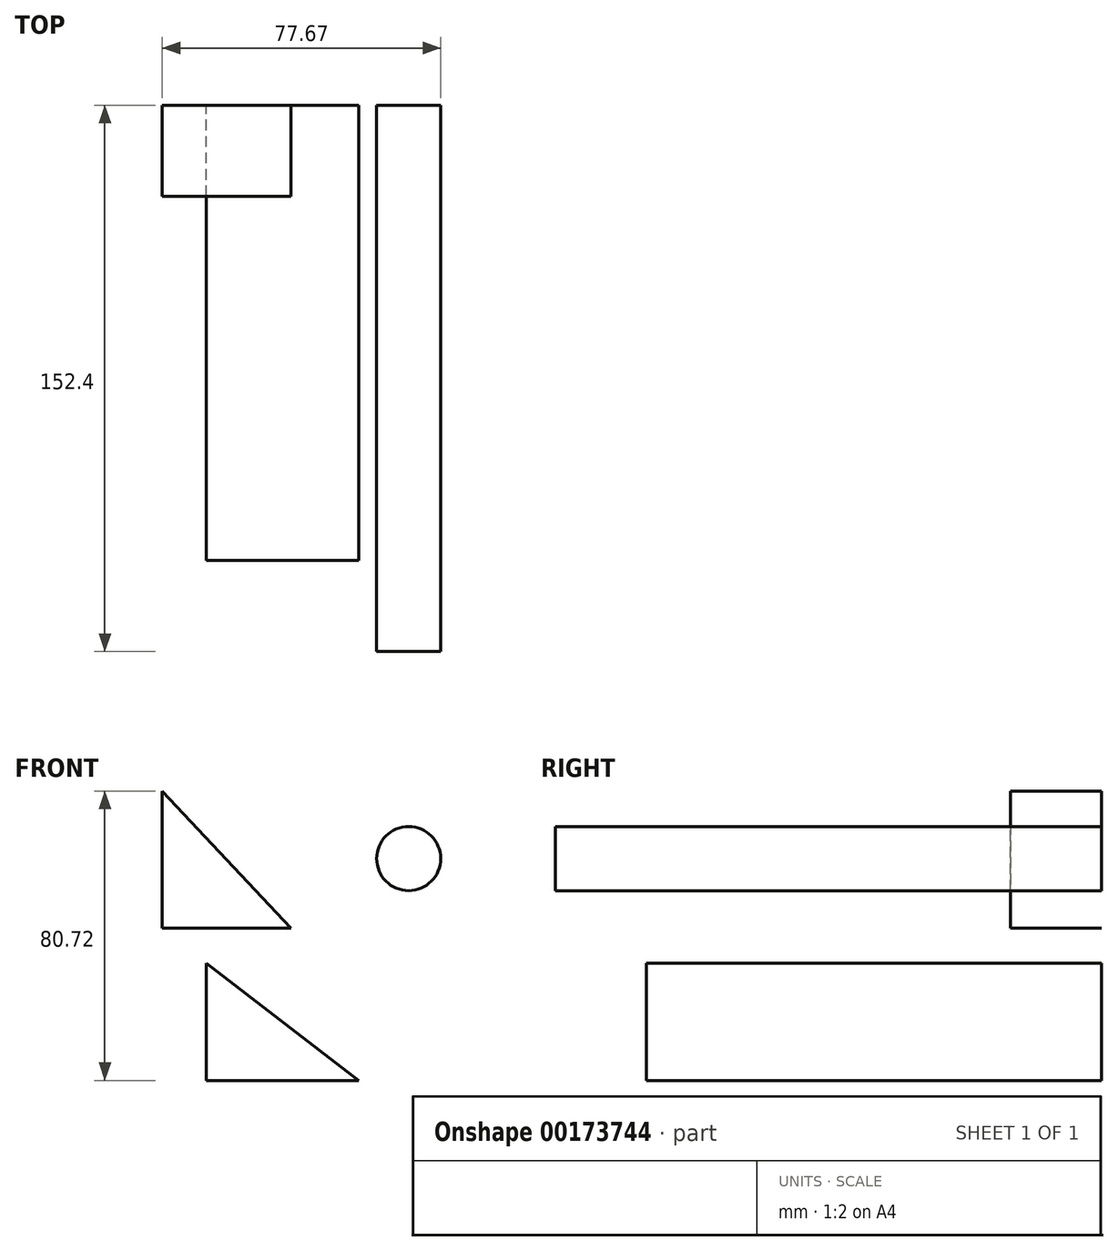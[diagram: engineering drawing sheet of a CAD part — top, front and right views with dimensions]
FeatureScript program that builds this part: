
annotation { "Feature Type Name" : "Feature", "Feature Type Description" : "" }
export const myFeature = defineFeature(function(context is Context, id is Id, definition is map)
    precondition{}
    {
        {
            var Q0;
            Q0=qCreatedBy(makeId("Front.planeOp"),FACE);
            var sketch = newSketch(context, id + "F0", { "sketchPlane" : qUnion([Q0])});
            skCircle(sketch, "E0", {"center": v(0, 29.52) * mm, "radius": 26.41 * mm});
            skSolve(sketch);
        }
        {
            var Q0;
            Q0=makeQuery(id+"F0.imprint","IMPRINT",FACE,{"disambiguationData":[TD([[makeQuery(id+"F0.imprint","IMPRINT",EDGE,{"derivedFrom":sQuery(id+"F0.wireOp",EDGE,"E0")}),1.0]])]});
            var sketch = newSketch(context, id + "F1", { "sketchPlane" : qUnion([Q0])});
            skCircle(sketch, "E1", {"center": v(0, 29.24) * mm, "radius": 8.93 * mm});
            skSolve(sketch);
        }
        {
            var Q0;
            Q0 = qSketchRegion(id + "F1", true);
            extrude(context, id + "F2", {"entities" : qUnion([Q0]), "depth" : 25.4 * mm});
        }
        {
            var Q0;
            Q0=makeQuery(id+"F2.opExtrude","CAP_FACE",FACE,{"disambiguationData":[OSD([sQuery(id+"F1.wireOp",EDGE,"E1")])],"isStart":false});
            extrude(context, id + "F3", {"entities" : qUnion([Q0]), "operationType" : NewBodyOperationType.ADD, "depth" : 127 * mm});
        }
        {
            var Q0;
            Q0=qCreatedBy(makeId("Front.planeOp"),FACE);
            var sketch = newSketch(context, id + "F4", { "sketchPlane" : qUnion([Q0])});
            skLineSegment(sketch, "E2", {"start": v(-56.48, 0) * mm, "end": v(-56.48, -32.66) * mm});
            skLineSegment(sketch, "E3", {"start": v(-56.48, -32.66) * mm, "end": v(-13.98, -32.66) * mm});
            skLineSegment(sketch, "E4", {"start": v(-13.98, -32.66) * mm, "end": v(-56.48, 0) * mm});
            skSolve(sketch);
        }
        {
            var Q0;
            Q0 = qSketchRegion(id + "F4", true);
            extrude(context, id + "F5", {"entities" : qUnion([Q0]), "depth" : 127 * mm});
        }
        {
            var Q0;
            Q0=qCreatedBy(makeId("Front.planeOp"),FACE);
            var sketch = newSketch(context, id + "F6", { "sketchPlane" : qUnion([Q0])});
            skLineSegment(sketch, "E5", {"start": v(-68.74, 48.06) * mm, "end": v(-68.74, 9.84) * mm});
            skLineSegment(sketch, "E6", {"start": v(-68.74, 9.84) * mm, "end": v(-32.8, 9.84) * mm});
            skLineSegment(sketch, "E7", {"start": v(-32.8, 9.84) * mm, "end": v(-68.74, 48.06) * mm});
            skSolve(sketch);
        }
        {
            var Q0;
            Q0 = qSketchRegion(id + "F6", true);
            extrude(context, id + "F7", {"entities" : qUnion([Q0]), "depth" : 25.4 * mm});
        }
    });
